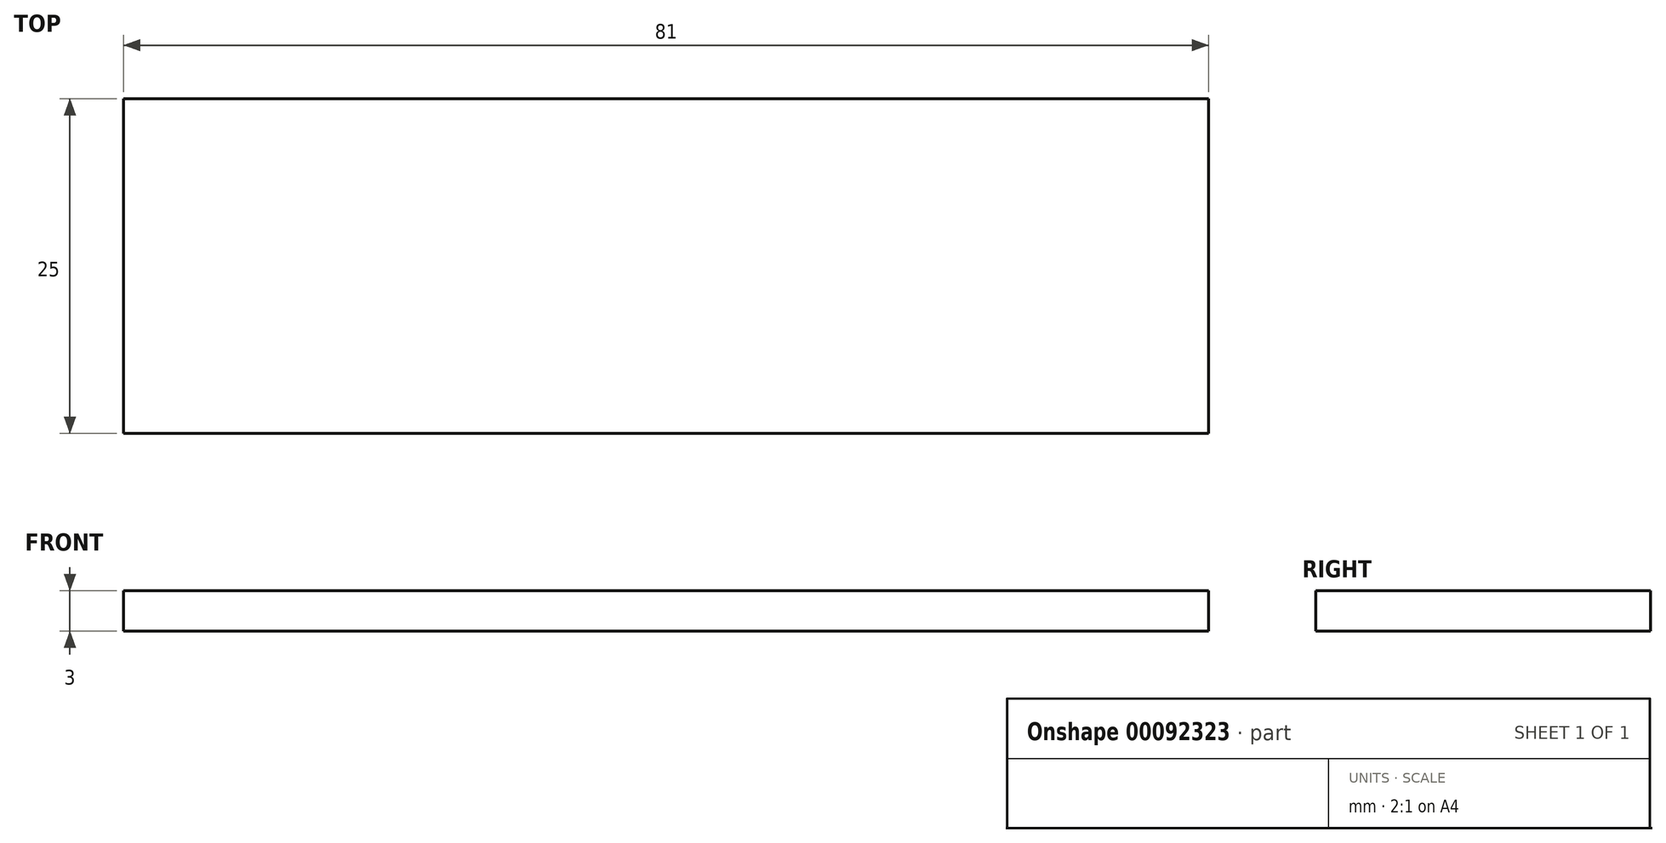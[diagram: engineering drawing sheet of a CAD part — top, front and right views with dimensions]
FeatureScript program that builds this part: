
annotation { "Feature Type Name" : "Feature", "Feature Type Description" : "" }
export const myFeature = defineFeature(function(context is Context, id is Id, definition is map)
    precondition{}
    {
        {
            var Q0;
            Q0=qCreatedBy(makeId("Top.planeOp"),FACE);
            var sketch = newSketch(context, id + "F0", { "sketchPlane" : qUnion([Q0])});
            skLineSegment(sketch, "E0.bottom", {"start": v(-40.5, 12.5) * mm, "end": v(40.5, 12.5) * mm});
            skLineSegment(sketch, "E0.top", {"start": v(-40.5, -12.5) * mm, "end": v(40.5, -12.5) * mm});
            skLineSegment(sketch, "E0.left", {"start": v(-40.5, 12.5) * mm, "end": v(-40.5, -12.5) * mm});
            skLineSegment(sketch, "E0.right", {"start": v(40.5, 12.5) * mm, "end": v(40.5, -12.5) * mm});
            skSolve(sketch);
        }
        {
            var Q0;
            Q0=makeQuery(id+"F0.imprint","IMPRINT",FACE,{"disambiguationData":[TD([[makeQuery(id+"F0.imprint","IMPRINT",EDGE,{"derivedFrom":sQuery(id+"F0.wireOp",EDGE,"E0.bottom")}),-1.0]])]});
            extrude(context, id + "F1", {"entities" : qUnion([Q0]), "endBound" : BoundingType.SYMMETRIC, "depth" : 3 * mm});
        }
    });
